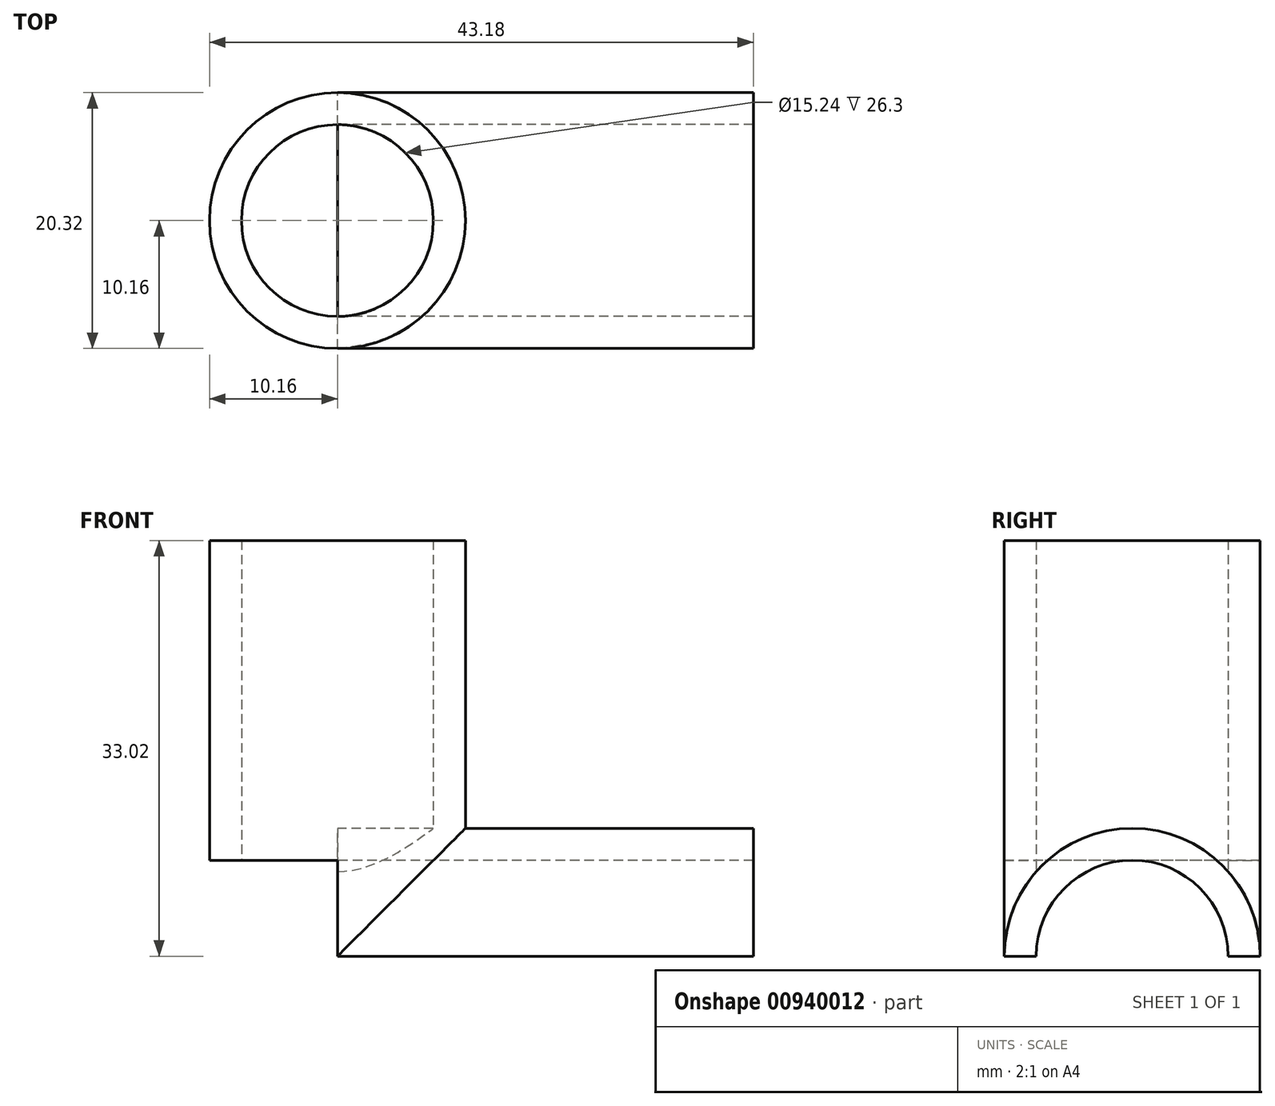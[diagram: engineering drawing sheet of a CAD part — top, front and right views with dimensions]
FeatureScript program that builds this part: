
annotation { "Feature Type Name" : "Feature", "Feature Type Description" : "" }
export const myFeature = defineFeature(function(context is Context, id is Id, definition is map)
    precondition{}
    {
        {
            var Q0;
            Q0=qCreatedBy(makeId("Top.planeOp"),FACE);
            var sketch = newSketch(context, id + "F0", { "sketchPlane" : qUnion([Q0])});
            skCircle(sketch, "E0", {"center": v(0, 0) * mm, "radius": 7.62 * mm});
            skCircle(sketch, "E1", {"center": v(0, 0) * mm, "radius": 10.16 * mm});
            skSolve(sketch);
        }
        {
            var Q0;
            Q0=makeQuery(id+"F0.imprint","IMPRINT",FACE,{"disambiguationData":[TD([[makeQuery(id+"F0.imprint","IMPRINT",EDGE,{"derivedFrom":sQuery(id+"F0.wireOp",EDGE,"E0")}),-1.0]])]});
            extrude(context, id + "F1", {"entities" : qUnion([Q0]), "depth" : 25.4 * mm, "offsetDistance" : 25.4 * mm});
        }
        {
            var Q0;
            Q0=qCreatedBy(makeId("Right.planeOp"),FACE);
            var sketch = newSketch(context, id + "F2", { "sketchPlane" : qUnion([Q0])});
            skArc(sketch, "E2", {"start": v(-7.59, 0) * mm, "mid": v(0, 7.59) * mm, "end": v(7.59, 0) * mm});
            skArc(sketch, "E3", {"start": v(-10.16, 0) * mm, "mid": v(0, 10.16) * mm, "end": v(10.16, 0) * mm});
            skLineSegment(sketch, "E4", {"start": v(-7.59, 0) * mm, "end": v(-10.16, 0) * mm});
            skLineSegment(sketch, "E5", {"start": v(7.59, 0) * mm, "end": v(10.16, 0) * mm});
            skSolve(sketch);
        }
        {
            var Q0;
            Q0 = qSketchRegion(id + "F2", true);
            extrude(context, id + "F3", {"entities" : qUnion([Q0]), "operationType" : NewBodyOperationType.ADD, "depth" : 25.4 * mm, "offsetDistance" : 25.4 * mm});
        }
        {
            var Q0;
            Q0=qCreatedBy(makeId("Right.planeOp"),FACE);
            var sketch = newSketch(context, id + "F4", { "sketchPlane" : qUnion([Q0])});
            skArc(sketch, "E6", {"start": v(-7.62, 0) * mm, "mid": v(0, 7.62) * mm, "end": v(7.62, 0) * mm});
            skLineSegment(sketch, "E7", {"start": v(-7.62, 0) * mm, "end": v(7.62, 0) * mm});
            skSolve(sketch);
        }
        {
            var Q0;
            Q0 = qSketchRegion(id + "F4", true);
            extrude(context, id + "F5", {"entities" : qUnion([Q0]), "operationType" : NewBodyOperationType.REMOVE, "depth" : 46.74 * mm, "offsetDistance" : 25.4 * mm});
        }
        {
            var Q0;
            Q0=makeQuery(id+"F3.boolean.opBoolean","MERGE",FACE,{"derivedFrom":[makeQuery(id+"F1.opExtrude","CAP_FACE",FACE,{"disambiguationData":[OSD([sQuery(id+"F0.wireOp",EDGE,"E0"),sQuery(id+"F0.wireOp",EDGE,"E1")])],"isStart":true}),makeQuery(id+"F3.opExtrude","SWEPT_FACE",FACE,{"disambiguationData":[OSD([sQuery(id+"F2.wireOp",EDGE,"E4")])]}),makeQuery(id+"F3.opExtrude","SWEPT_FACE",FACE,{"disambiguationData":[OSD([sQuery(id+"F2.wireOp",EDGE,"E5")])]})]});
            var sketch = newSketch(context, id + "F6", { "sketchPlane" : qUnion([Q0])});
            skLineSegment(sketch, "E8", {"start": v(0, 10.16) * mm, "end": v(0, -10.16) * mm});
            skSolve(sketch);
        }
        {
            var Q0;
            {var subQ3=sQuery(id+"F0.wireOp",EDGE,"E1");var subQ4=sQuery(id+"F2.wireOp",EDGE,"E3");var subQ9=makeQuery(id+"F3.boolean.opBoolean","SPLIT",EDGE,{"disambiguationData":[TD([makeQuery(id+"F3.opExtrude","SWEPT_FACE",FACE,{"disambiguationData":[OSD([subQ4])]})])],"derivedFrom":makeQuery(id+"F1.opExtrude","CAP_EDGE",EDGE,{"disambiguationData":[OSD([subQ3])],"isStart":true})});Q0=makeQuery(id+"F6.imprint","IMPRINT",FACE,{"disambiguationData":[TD([[makeQuery(id+"F6.imprint","IMPRINT",EDGE,{"derivedFrom":subQ9}),-1.0]])]});}
            extrude(context, id + "F7", {"entities" : qUnion([Q0]), "operationType" : NewBodyOperationType.REMOVE, "oppositeDirection" : true, "depth" : 7.62 * mm, "offsetDistance" : 25.4 * mm});
        }
        {
            var Q0;
            Q0=makeQuery(id+"F1.opExtrude","CAP_FACE",FACE,{"disambiguationData":[OSD([sQuery(id+"F0.wireOp",EDGE,"E0"),sQuery(id+"F0.wireOp",EDGE,"E1")])],"isStart":false});
            extrude(context, id + "F8", {"entities" : qUnion([Q0]), "operationType" : NewBodyOperationType.ADD, "depth" : 7.62 * mm, "offsetDistance" : 25.4 * mm});
        }
        {
            var Q0;
            Q0=makeQuery(id+"F3.opExtrude","CAP_FACE",FACE,{"disambiguationData":[OSD([sQuery(id+"F2.wireOp",EDGE,"E2"),sQuery(id+"F2.wireOp",EDGE,"E3"),sQuery(id+"F2.wireOp",EDGE,"E4"),sQuery(id+"F2.wireOp",EDGE,"E5")])],"isStart":false});
            extrude(context, id + "F9", {"entities" : qUnion([Q0]), "operationType" : NewBodyOperationType.ADD, "depth" : 7.62 * mm, "offsetDistance" : 25.4 * mm});
        }
    });
